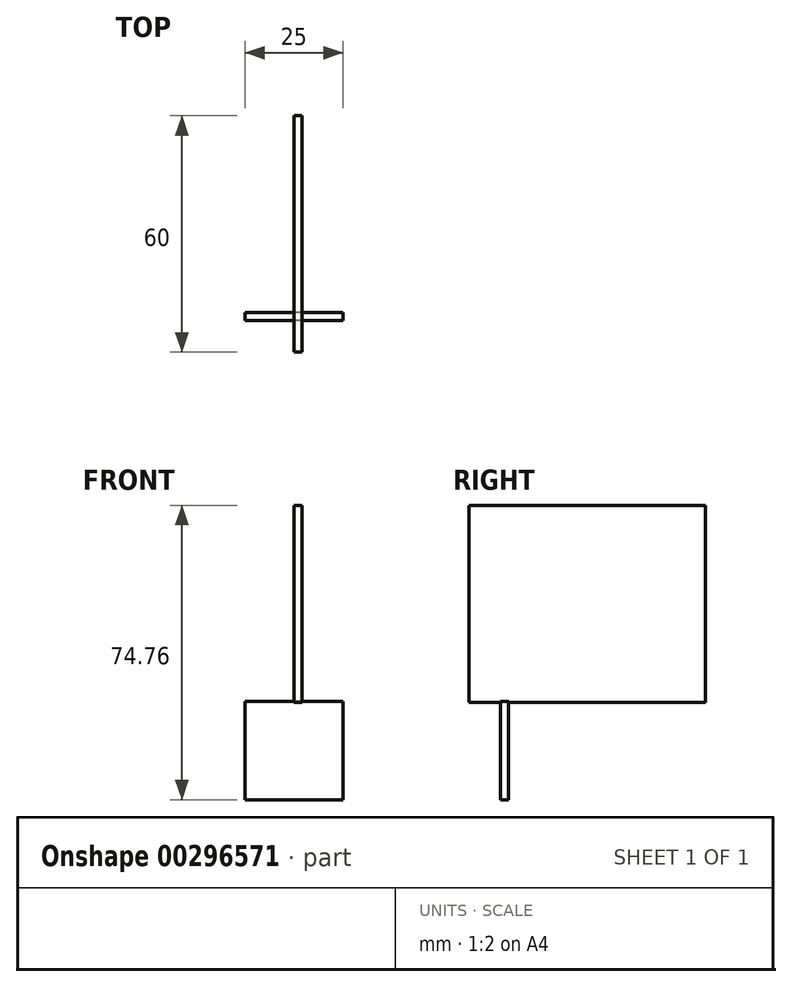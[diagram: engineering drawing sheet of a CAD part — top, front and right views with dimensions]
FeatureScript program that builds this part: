
annotation { "Feature Type Name" : "Feature", "Feature Type Description" : "" }
export const myFeature = defineFeature(function(context is Context, id is Id, definition is map)
    precondition{}
    {
        {
            var Q0;
            Q0=qCreatedBy(makeId("Front.planeOp"),FACE);
            var sketch = newSketch(context, id + "F0", { "sketchPlane" : qUnion([Q0])});
            skLineSegment(sketch, "E0.bottom", {"start": v(12.5, 12.5) * mm, "end": v(-12.5, 12.5) * mm});
            skLineSegment(sketch, "E0.top", {"start": v(12.5, -12.5) * mm, "end": v(-12.5, -12.5) * mm});
            skLineSegment(sketch, "E0.left", {"start": v(12.5, 12.5) * mm, "end": v(12.5, -12.5) * mm});
            skLineSegment(sketch, "E0.right", {"start": v(-12.5, 12.5) * mm, "end": v(-12.5, -12.5) * mm});
            skPoint(sketch, "E0.middle", {"position": v(0, 0) * mm});
            skSolve(sketch);
        }
        {
            var Q0;
            Q0=makeQuery(id+"F0.imprint","IMPRINT",FACE,{"disambiguationData":[TD([[makeQuery(id+"F0.imprint","IMPRINT",EDGE,{"derivedFrom":sQuery(id+"F0.wireOp",EDGE,"E0.bottom")}),1.0]])]});
            extrude(context, id + "F1", {"entities" : qUnion([Q0]), "depth" : 2 * mm});
        }
        {
            var Q0;
            Q0=qCreatedBy(makeId("Right.planeOp"),FACE);
            var sketch = newSketch(context, id + "F2", { "sketchPlane" : qUnion([Q0])});
            skLineSegment(sketch, "E1", {"start": v(0, 12.26) * mm, "end": v(-10, 12.26) * mm});
            skLineSegment(sketch, "E2", {"start": v(-10, 12.26) * mm, "end": v(-10, 62.26) * mm});
            skLineSegment(sketch, "E3", {"start": v(-10, 62.26) * mm, "end": v(50, 62.26) * mm});
            skLineSegment(sketch, "E4", {"start": v(50, 62.26) * mm, "end": v(50, 12.26) * mm});
            skLineSegment(sketch, "E5", {"start": v(50, 12.26) * mm, "end": v(0, 12.26) * mm});
            skSolve(sketch);
        }
        {
            var Q0;
            Q0=makeQuery(id+"F2.imprint","IMPRINT",FACE,{"disambiguationData":[TD([[makeQuery(id+"F2.imprint","IMPRINT",EDGE,{"derivedFrom":sQuery(id+"F2.wireOp",EDGE,"E1")}),-1.0]])]});
            extrude(context, id + "F3", {"entities" : qUnion([Q0]), "depth" : 2 * mm});
        }
    });
